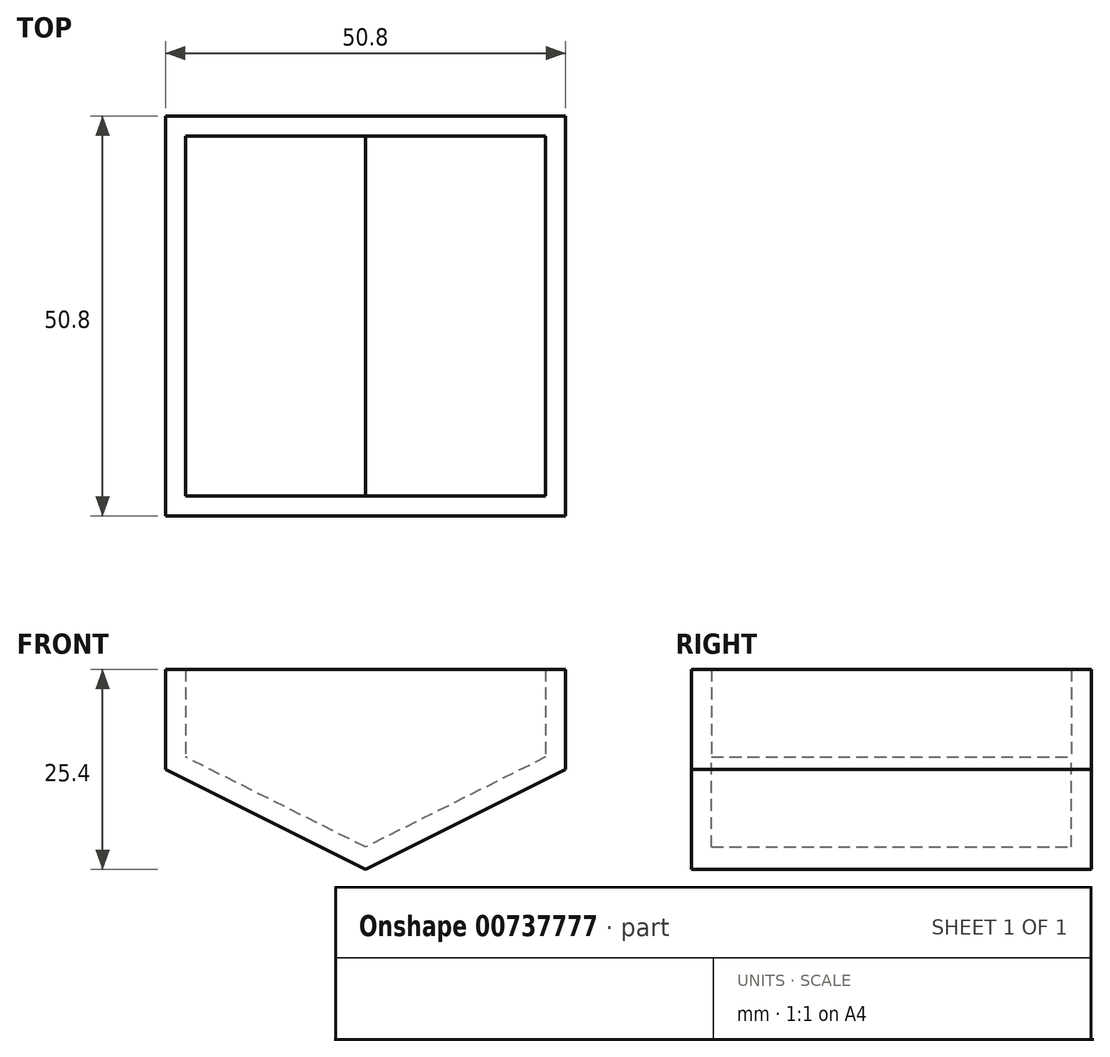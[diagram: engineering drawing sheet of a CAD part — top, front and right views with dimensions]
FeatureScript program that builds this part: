
annotation { "Feature Type Name" : "Feature", "Feature Type Description" : "" }
export const myFeature = defineFeature(function(context is Context, id is Id, definition is map)
    precondition{}
    {
        {
            var Q0;
            Q0=qCreatedBy(makeId("Front.planeOp"),FACE);
            var sketch = newSketch(context, id + "F0", { "sketchPlane" : qUnion([Q0])});
            skLineSegment(sketch, "E0", {"start": v(0, 0) * mm, "end": v(25.4, 0) * mm});
            skLineSegment(sketch, "E1", {"start": v(25.4, 0) * mm, "end": v(0, 0) * mm});
            skLineSegment(sketch, "E2", {"start": v(0, 0) * mm, "end": v(-25.4, 0) * mm});
            skLineSegment(sketch, "E3", {"start": v(-25.4, 0) * mm, "end": v(-25.4, -12.7) * mm});
            skLineSegment(sketch, "E4", {"start": v(25.4, 0) * mm, "end": v(25.4, -12.7) * mm});
            skLineSegment(sketch, "E5", {"start": v(0, 0) * mm, "end": v(0, -25.4) * mm});
            skLineSegment(sketch, "E6", {"start": v(0, -25.4) * mm, "end": v(-25.4, -12.7) * mm});
            skLineSegment(sketch, "E7", {"start": v(25.4, -12.7) * mm, "end": v(0, -25.4) * mm});
            skSolve(sketch);
        }
        {
            var Q0;
            Q0 = qSketchRegion(id + "F0", true);
            extrude(context, id + "F1", {"entities" : qUnion([Q0]), "depth" : 50.8 * mm, "offsetDistance" : 25.4 * mm});
        }
        {
            var Q0;
            Q0=makeQuery(id+"F1.opExtrude","SWEPT_FACE",FACE,{"disambiguationData":[OSD([sQuery(id+"F0.wireOp",EDGE,"E1"),sQuery(id+"F0.wireOp",EDGE,"E2")])]});
            shell(context, id + "F2", {"entities" : qUnion([Q0]), "thickness" : 2.54 * mm});
        }
    });
